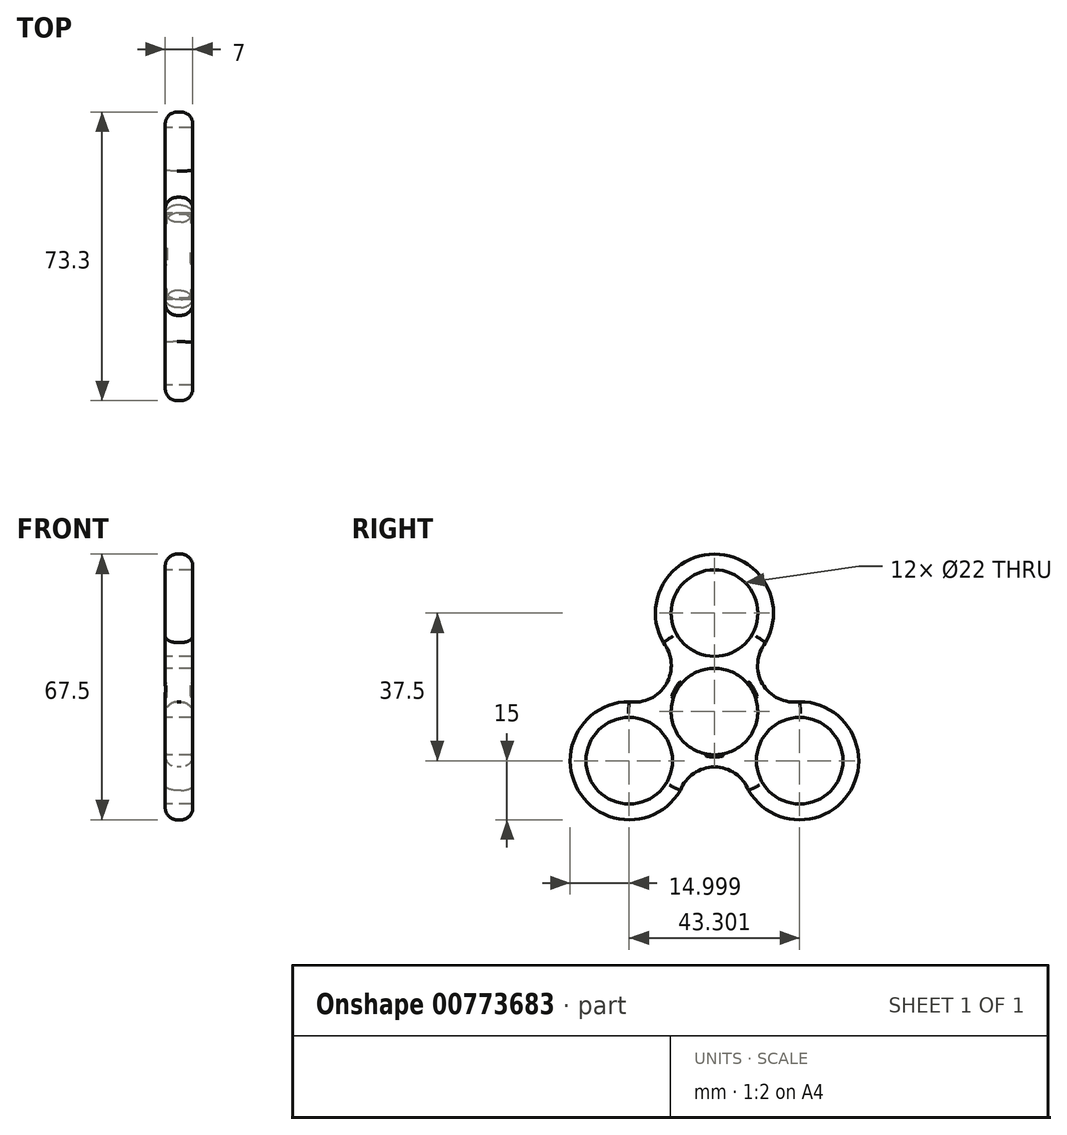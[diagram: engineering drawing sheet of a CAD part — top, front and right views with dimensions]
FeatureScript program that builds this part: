
annotation { "Feature Type Name" : "Feature", "Feature Type Description" : "" }
export const myFeature = defineFeature(function(context is Context, id is Id, definition is map)
    precondition{}
    {
        {
            var Q0;
            Q0=qCreatedBy(makeId("Right.planeOp"),FACE);
            var sketch = newSketch(context, id + "F0", { "sketchPlane" : qUnion([Q0])});
            skLineSegment(sketch, "E0", {"start": v(0, 0) * mm, "end": v(0, 25) * mm, "construction": true});
            skCircle(sketch, "E1", {"center": v(0, 25) * mm, "radius": 15 * mm});
            skCircle(sketch, "E2.1.0", {"center": v(-21.65, -12.5) * mm, "radius": 15 * mm});
            skCircle(sketch, "E2.2.0", {"center": v(21.65, -12.5) * mm, "radius": 15 * mm});
            skPoint(sketch, "E2.center", {"position": v(0, 0) * mm});
            skLineSegment(sketch, "E3", {"start": v(0, 25) * mm, "end": v(-21.65, -12.5) * mm, "construction": true});
            skLineSegment(sketch, "E4", {"start": v(-13, 17.53) * mm, "end": v(-21.69, 2.5) * mm, "construction": true});
            skArc(sketch, "E5", {"start": v(-21.69, 2.5) * mm, "mid": v(-12.21, 7.05) * mm, "end": v(-13, 17.53) * mm});
            skArc(sketch, "E6.1.0", {"start": v(8.68, -20.03) * mm, "mid": v(0, -14.1) * mm, "end": v(-8.68, -20.03) * mm});
            skArc(sketch, "E6.2.0", {"start": v(13, 17.53) * mm, "mid": v(12.21, 7.05) * mm, "end": v(21.69, 2.5) * mm});
            skCircle(sketch, "E7", {"center": v(0, 0) * mm, "radius": 11 * mm});
            skCircle(sketch, "E8", {"center": v(-21.65, -12.5) * mm, "radius": 11 * mm});
            skCircle(sketch, "E9.1.0", {"center": v(21.65, -12.5) * mm, "radius": 11 * mm});
            skCircle(sketch, "E9.2.0", {"center": v(0, 25) * mm, "radius": 11 * mm});
            skSolve(sketch);
        }
        {
            var Q0;
            Q0=makeQuery(id+"F0.imprint","IMPRINT",FACE,{"disambiguationData":[TD([[makeQuery(id+"F0.imprint","IMPRINT",EDGE,{"derivedFrom":sQuery(id+"F0.wireOp",EDGE,"E8")}),-1.0]])]});
            var Q1;
            {var subQ0=sQuery(id+"F0.wireOp",EDGE,"E5");var subQ1=sQuery(id+"F0.wireOp",EDGE,"E1");var subQ2=makeQuery(id+"F0.imprint","INTERSECT",VERTEX,{"disambiguationData":[OD(1.0)],"derivedFrom":[subQ1,subQ0]});Q1=makeQuery(id+"F0.imprint","IMPRINT",FACE,{"disambiguationData":[TD([[makeQuery(id+"F0.imprint","IMPRINT",EDGE,{"disambiguationData":[TD([[subQ2,-1.0]])],"derivedFrom":subQ1}),-1.0]])]});}
            var Q2;
            {var subQ0=sQuery(id+"F0.wireOp",EDGE,"E6.1.0");var subQ1=sQuery(id+"F0.wireOp",EDGE,"E2.1.0");var subQ2=makeQuery(id+"F0.imprint","INTERSECT",VERTEX,{"disambiguationData":[OD(1.0)],"derivedFrom":[subQ1,subQ0]});Q2=makeQuery(id+"F0.imprint","IMPRINT",FACE,{"disambiguationData":[TD([[makeQuery(id+"F0.imprint","IMPRINT",EDGE,{"disambiguationData":[TD([[subQ2,-1.0]])],"derivedFrom":subQ1}),-1.0]])]});}
            var Q3;
            Q3=makeQuery(id+"F0.imprint","IMPRINT",FACE,{"disambiguationData":[TD([[makeQuery(id+"F0.imprint","IMPRINT",EDGE,{"derivedFrom":sQuery(id+"F0.wireOp",EDGE,"E9.1.0")}),-1.0]])]});
            var Q4;
            Q4=makeQuery(id+"F0.imprint","IMPRINT",FACE,{"disambiguationData":[TD([[makeQuery(id+"F0.imprint","IMPRINT",EDGE,{"derivedFrom":sQuery(id+"F0.wireOp",EDGE,"E9.2.0")}),-1.0]])]});
            var Q5;
            {var subQ0=sQuery(id+"F0.wireOp",EDGE,"E6.2.0");var subQ1=sQuery(id+"F0.wireOp",EDGE,"E1");var subQ2=makeQuery(id+"F0.imprint","INTERSECT",VERTEX,{"disambiguationData":[OD(1.0)],"derivedFrom":[subQ1,subQ0]});Q5=makeQuery(id+"F0.imprint","IMPRINT",FACE,{"disambiguationData":[TD([[makeQuery(id+"F0.imprint","IMPRINT",EDGE,{"disambiguationData":[TD([[subQ2,1.0]])],"derivedFrom":subQ1}),-1.0]])]});}
            extrude(context, id + "F1", {"entities" : qUnion([Q0, Q1, Q2, Q3, Q4, Q5]), "depth" : 7 * mm, "offsetDistance" : 25.4 * mm});
        }
        {
            var Q0;
            Q0=makeQuery(id+"F1.opExtrude","CAP_EDGE",EDGE,{"disambiguationData":[OSD([sQuery(id+"F0.wireOp",EDGE,"E2.1.0")])],"isStart":false});
            var Q1;
            Q1=makeQuery(id+"F1.opExtrude","CAP_EDGE",EDGE,{"disambiguationData":[OSD([sQuery(id+"F0.wireOp",EDGE,"E5")])],"isStart":false});
            var Q2;
            Q2=makeQuery(id+"F1.opExtrude","CAP_EDGE",EDGE,{"disambiguationData":[OSD([sQuery(id+"F0.wireOp",EDGE,"E1")])],"isStart":false});
            var Q3;
            Q3=makeQuery(id+"F1.opExtrude","CAP_EDGE",EDGE,{"disambiguationData":[OSD([sQuery(id+"F0.wireOp",EDGE,"E6.2.0")])],"isStart":false});
            var Q4;
            Q4=makeQuery(id+"F1.opExtrude","CAP_EDGE",EDGE,{"disambiguationData":[OSD([sQuery(id+"F0.wireOp",EDGE,"E6.1.0")])],"isStart":false});
            var Q5;
            Q5=makeQuery(id+"F1.opExtrude","CAP_EDGE",EDGE,{"disambiguationData":[OSD([sQuery(id+"F0.wireOp",EDGE,"E2.2.0")])],"isStart":false});
            var Q6;
            Q6=makeQuery(id+"F1.opExtrude","CAP_EDGE",EDGE,{"disambiguationData":[OSD([sQuery(id+"F0.wireOp",EDGE,"E5")])],"isStart":true});
            var Q7;
            Q7=makeQuery(id+"F1.opExtrude","CAP_EDGE",EDGE,{"disambiguationData":[OSD([sQuery(id+"F0.wireOp",EDGE,"E1")])],"isStart":true});
            var Q8;
            Q8=makeQuery(id+"F1.opExtrude","CAP_EDGE",EDGE,{"disambiguationData":[OSD([sQuery(id+"F0.wireOp",EDGE,"E2.1.0")])],"isStart":true});
            var Q9;
            Q9=makeQuery(id+"F1.opExtrude","CAP_EDGE",EDGE,{"disambiguationData":[OSD([sQuery(id+"F0.wireOp",EDGE,"E6.2.0")])],"isStart":true});
            var Q10;
            Q10=makeQuery(id+"F1.opExtrude","CAP_EDGE",EDGE,{"disambiguationData":[OSD([sQuery(id+"F0.wireOp",EDGE,"E2.2.0")])],"isStart":true});
            var Q11;
            Q11=makeQuery(id+"F1.opExtrude","CAP_EDGE",EDGE,{"disambiguationData":[OSD([sQuery(id+"F0.wireOp",EDGE,"E6.1.0")])],"isStart":true});
            fillet(context, id + "F2", {"entities" : qUnion([Q0, Q1, Q2, Q3, Q4, Q5, Q6, Q7, Q8, Q9, Q10, Q11]), "radius" : 3 * mm, "tangentPropagation" : true, "allowEdgeOverflow" : false});
        }
        {
            var Q0;
            Q0=makeQuery(id+"F1.opExtrude","CAP_EDGE",EDGE,{"disambiguationData":[OSD([sQuery(id+"F0.wireOp",EDGE,"E7")])],"isStart":true});
            var Q1;
            Q1=makeQuery(id+"F1.opExtrude","CAP_EDGE",EDGE,{"disambiguationData":[OSD([sQuery(id+"F0.wireOp",EDGE,"E9.2.0")])],"isStart":true});
            var Q2;
            Q2=makeQuery(id+"F1.opExtrude","CAP_EDGE",EDGE,{"disambiguationData":[OSD([sQuery(id+"F0.wireOp",EDGE,"E8")])],"isStart":true});
            var Q3;
            Q3=makeQuery(id+"F1.opExtrude","CAP_EDGE",EDGE,{"disambiguationData":[OSD([sQuery(id+"F0.wireOp",EDGE,"E9.1.0")])],"isStart":true});
            var Q4;
            Q4=makeQuery(id+"F1.opExtrude","CAP_EDGE",EDGE,{"disambiguationData":[OSD([sQuery(id+"F0.wireOp",EDGE,"E9.2.0")])],"isStart":false});
            var Q5;
            Q5=makeQuery(id+"F1.opExtrude","CAP_EDGE",EDGE,{"disambiguationData":[OSD([sQuery(id+"F0.wireOp",EDGE,"E7")])],"isStart":false});
            var Q6;
            Q6=makeQuery(id+"F1.opExtrude","CAP_EDGE",EDGE,{"disambiguationData":[OSD([sQuery(id+"F0.wireOp",EDGE,"E8")])],"isStart":false});
            var Q7;
            Q7=makeQuery(id+"F1.opExtrude","CAP_EDGE",EDGE,{"disambiguationData":[OSD([sQuery(id+"F0.wireOp",EDGE,"E9.1.0")])],"isStart":false});
            fillet(context, id + "F3", {"entities" : qUnion([Q0, Q1, Q2, Q3, Q4, Q5, Q6, Q7]), "radius" : .5 * mm, "tangentPropagation" : true, "allowEdgeOverflow" : false});
        }
    });
